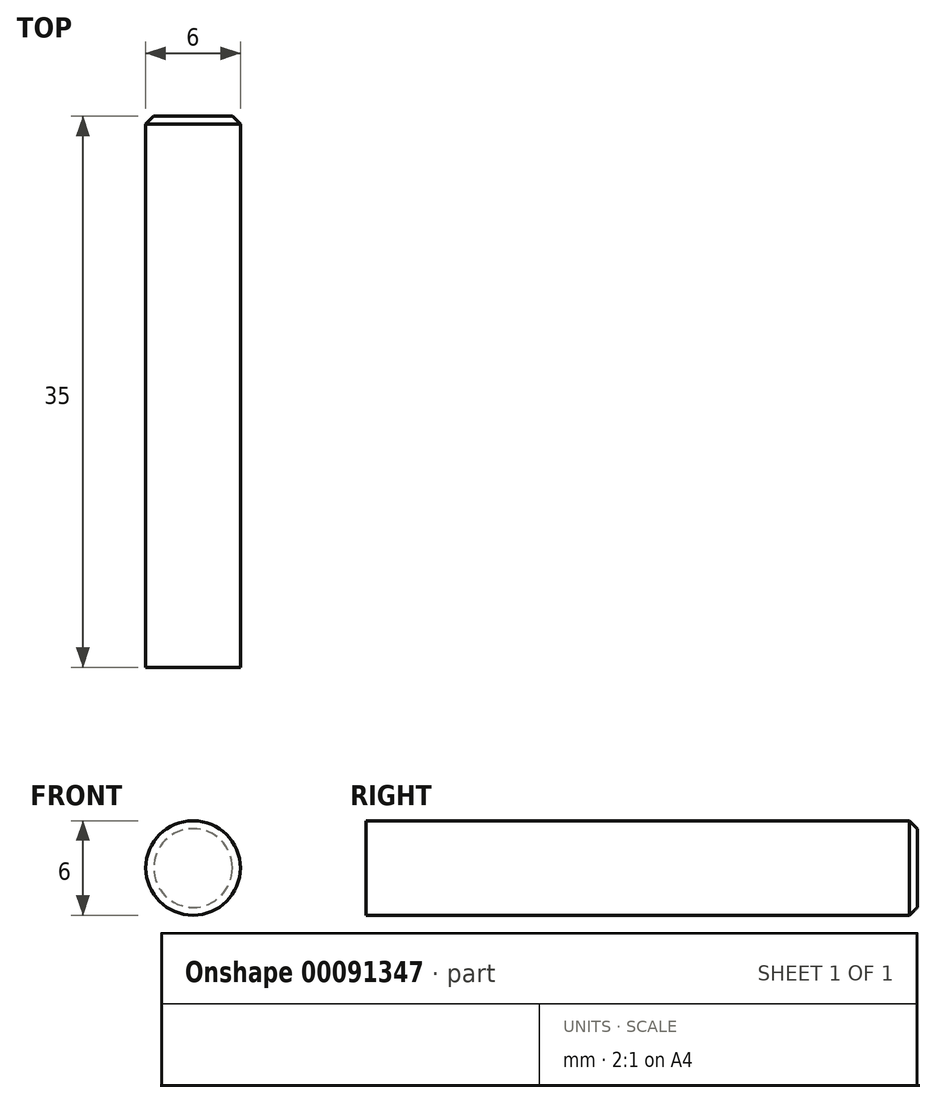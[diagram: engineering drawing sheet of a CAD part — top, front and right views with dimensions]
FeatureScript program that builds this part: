
annotation { "Feature Type Name" : "Feature", "Feature Type Description" : "" }
export const myFeature = defineFeature(function(context is Context, id is Id, definition is map)
    precondition{}
    {
        {
            var Q0;
            Q0=qCreatedBy(makeId("Front.planeOp"),FACE);
            var sketch = newSketch(context, id + "F0", { "sketchPlane" : qUnion([Q0])});
            skCircle(sketch, "E0", {"center": v(0, 0) * mm, "radius": 3 * mm});
            skSolve(sketch);
        }
        {
            var Q0;
            Q0=makeQuery(id+"F0.imprint","IMPRINT",FACE,{"disambiguationData":[TD([[makeQuery(id+"F0.imprint","IMPRINT",EDGE,{"derivedFrom":sQuery(id+"F0.wireOp",EDGE,"E0")}),1.0]])]});
            extrude(context, id + "F1", {"entities" : qUnion([Q0]), "oppositeDirection" : true, "depth" : 35 * mm});
        }
        {
            var Q0;
            Q0=makeQuery(id+"F1.opExtrude","CAP_EDGE",EDGE,{"disambiguationData":[OSD([sQuery(id+"F0.wireOp",EDGE,"E0")])],"isStart":false});
            chamfer(context, id + "F2", {"entities" : qUnion([Q0]), "width" : .5 * mm, "tangentPropagation" : true});
        }
    });
